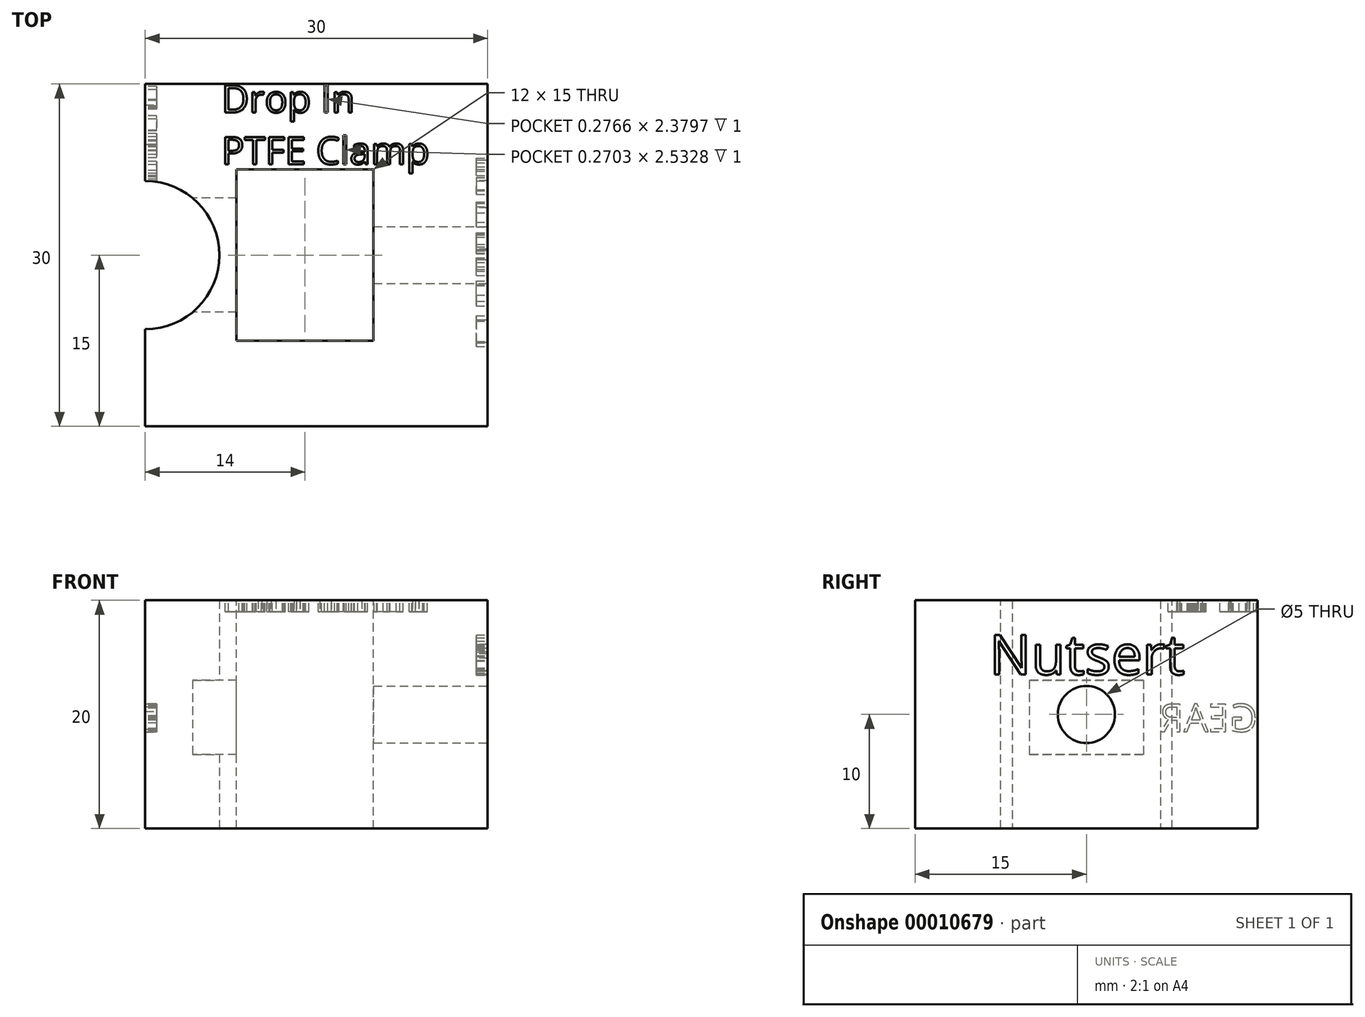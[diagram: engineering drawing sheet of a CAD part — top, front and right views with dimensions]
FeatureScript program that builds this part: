
annotation { "Feature Type Name" : "Feature", "Feature Type Description" : "" }
export const myFeature = defineFeature(function(context is Context, id is Id, definition is map)
    precondition{}
    {
        {
            var Q0;
            Q0=qCreatedBy(makeId("Top.planeOp"),FACE);
            var sketch = newSketch(context, id + "F0", { "sketchPlane" : qUnion([Q0])});
            skLineSegment(sketch, "E0.bottom", {"start": v(-15, 15) * mm, "end": v(15, 15) * mm});
            skLineSegment(sketch, "E0.top", {"start": v(-15, -15) * mm, "end": v(15, -15) * mm});
            skLineSegment(sketch, "E0.right", {"start": v(15, 15) * mm, "end": v(15, -15) * mm});
            skArc(sketch, "E1", {"start": v(-8.5, 0) * mm, "mid": v(-10.4, 4.6) * mm, "end": v(-15, 6.5) * mm});
            skArc(sketch, "E2", {"start": v(-15, -6.5) * mm, "mid": v(-10.4, -4.6) * mm, "end": v(-8.5, 0) * mm});
            skLineSegment(sketch, "E3", {"start": v(-15, 15) * mm, "end": v(-15, 6.5) * mm});
            skLineSegment(sketch, "E4", {"start": v(-15, -15) * mm, "end": v(-15, -6.5) * mm});
            skSolve(sketch);
        }
        {
            var Q0;
            Q0 = qSketchRegion(id + "F0", true);
            extrude(context, id + "F1", {"entities" : qUnion([Q0]), "depth" : 20 * mm});
        }
        {
            var Q0;
            Q0=makeQuery(id+"F1.opExtrude","CAP_FACE",FACE,{"disambiguationData":[OSD([sQuery(id+"F0.wireOp",EDGE,"E0.bottom"),sQuery(id+"F0.wireOp",EDGE,"E0.top"),sQuery(id+"F0.wireOp",EDGE,"E0.right"),sQuery(id+"F0.wireOp",EDGE,"E1"),sQuery(id+"F0.wireOp",EDGE,"E2"),sQuery(id+"F0.wireOp",EDGE,"E3"),sQuery(id+"F0.wireOp",EDGE,"E4")])],"isStart":false});
            var sketch = newSketch(context, id + "F2", { "sketchPlane" : qUnion([Q0])});
            skLineSegment(sketch, "E5.bottom", {"start": v(-7, 7.5) * mm, "end": v(5, 7.5) * mm});
            skLineSegment(sketch, "E5.top", {"start": v(-7, -7.5) * mm, "end": v(5, -7.5) * mm});
            skLineSegment(sketch, "E5.left", {"start": v(-7, 7.5) * mm, "end": v(-7, -7.5) * mm});
            skLineSegment(sketch, "E5.right", {"start": v(5, 7.5) * mm, "end": v(5, -7.5) * mm});
            skSolve(sketch);
        }
        {
            var Q0;
            Q0 = qSketchRegion(id + "F2", true);
            extrude(context, id + "F3", {"entities" : qUnion([Q0]), "operationType" : NewBodyOperationType.REMOVE, "endBound" : BoundingType.THROUGH_ALL, "oppositeDirection" : true, "depth" : 25 * mm});
        }
        {
            var Q0;
            Q0=makeQuery(id+"F1.opExtrude","SWEPT_FACE",FACE,{"disambiguationData":[OSD([sQuery(id+"F0.wireOp",EDGE,"E0.right")])]});
            var sketch = newSketch(context, id + "F4", { "sketchPlane" : qUnion([Q0])});
            skCircle(sketch, "E6", {"center": v(0, 10) * mm, "radius": 2.5 * mm});
            skSolve(sketch);
        }
        {
            var Q0;
            Q0 = qSketchRegion(id + "F4", true);
            var Q1;
            Q1=makeQuery(id+"F3.boolean.opBoolean","COPY",FACE,{"derivedFrom":makeQuery(id+"F3.opExtrude","SWEPT_FACE",FACE,{"disambiguationData":[OSD([sQuery(id+"F2.wireOp",EDGE,"E5.right")])]})});
            extrude(context, id + "F5", {"entities" : qUnion([Q0]), "operationType" : NewBodyOperationType.REMOVE, "endBound" : BoundingType.UP_TO_SURFACE, "oppositeDirection" : true, "endBoundEntityFace" : qUnion([Q1]), "depth" : 25 * mm});
        }
        {
            var Q0;
            Q0=makeQuery(id+"F1.opExtrude","SWEPT_FACE",FACE,{"disambiguationData":[OSD([sQuery(id+"F0.wireOp",EDGE,"E3")])]});
            var sketch = newSketch(context, id + "F6", { "sketchPlane" : qUnion([Q0])});
            skLineSegment(sketch, "E7.bottom", {"start": v(-5, 13) * mm, "end": v(5, 13) * mm});
            skLineSegment(sketch, "E7.top", {"start": v(-5, 6.5) * mm, "end": v(5, 6.5) * mm});
            skLineSegment(sketch, "E7.left", {"start": v(-5, 13) * mm, "end": v(-5, 6.5) * mm});
            skLineSegment(sketch, "E7.right", {"start": v(5, 13) * mm, "end": v(5, 6.5) * mm});
            skSolve(sketch);
        }
        {
            var Q0;
            Q0 = qSketchRegion(id + "F6", true);
            var Q1;
            Q1=makeQuery(id+"F3.boolean.opBoolean","COPY",FACE,{"derivedFrom":makeQuery(id+"F3.opExtrude","SWEPT_FACE",FACE,{"disambiguationData":[OSD([sQuery(id+"F2.wireOp",EDGE,"E5.left")])]})});
            extrude(context, id + "F7", {"entities" : qUnion([Q0]), "operationType" : NewBodyOperationType.REMOVE, "endBound" : BoundingType.UP_TO_SURFACE, "oppositeDirection" : true, "endBoundEntityFace" : qUnion([Q1]), "depth" : 25 * mm});
        }
        {
            var Q0;
            Q0=makeQuery(id+"F1.opExtrude","SWEPT_FACE",FACE,{"disambiguationData":[OSD([sQuery(id+"F0.wireOp",EDGE,"E0.right")])]});
            var sketch = newSketch(context, id + "F8", { "sketchPlane" : qUnion([Q0])});
            skText(sketch, "E8", { "text": "Nutsert\n", "fontName": "OpenSans-Regular.ttf"});
            const initialGuessF8  = {"E8": [-0.0085, 0.0135, 1, 0, 0.0035]};
            skSetInitialGuess(sketch, initialGuessF8);
            skSolve(sketch);
        }
        {
            var Q0;
            Q0 = qSketchRegion(id + "F8", true);
            extrude(context, id + "F9", {"entities" : qUnion([Q0]), "operationType" : NewBodyOperationType.REMOVE, "oppositeDirection" : true, "depth" : 1 * mm});
        }
        {
            var Q0;
            Q0=makeQuery(id+"F1.opExtrude","SWEPT_FACE",FACE,{"disambiguationData":[OSD([sQuery(id+"F0.wireOp",EDGE,"E3")])]});
            var sketch = newSketch(context, id + "F10", { "sketchPlane" : qUnion([Q0])});
            skText(sketch, "E9", { "text": "GEAR", "fontName": "OpenSans-Regular.ttf"});
            const initialGuessF10  = {"E9": [-0.015, 0.0085, 1, 0, 0.00243]};
            skSetInitialGuess(sketch, initialGuessF10);
            skSolve(sketch);
        }
        {
            var Q0;
            Q0 = qSketchRegion(id + "F10", true);
            extrude(context, id + "F11", {"entities" : qUnion([Q0]), "operationType" : NewBodyOperationType.REMOVE, "oppositeDirection" : true, "depth" : 1 * mm});
        }
        {
            var Q0;
            Q0=makeQuery(id+"F1.opExtrude","CAP_FACE",FACE,{"disambiguationData":[OSD([sQuery(id+"F0.wireOp",EDGE,"E0.bottom"),sQuery(id+"F0.wireOp",EDGE,"E0.top"),sQuery(id+"F0.wireOp",EDGE,"E0.right"),sQuery(id+"F0.wireOp",EDGE,"E1"),sQuery(id+"F0.wireOp",EDGE,"E2"),sQuery(id+"F0.wireOp",EDGE,"E3"),sQuery(id+"F0.wireOp",EDGE,"E4")])],"isStart":false});
            var sketch = newSketch(context, id + "F12", { "sketchPlane" : qUnion([Q0])});
            skText(sketch, "E10", { "text": "Drop In \nPTFE Clamp", "fontName": "OpenSans-Regular.ttf"});
            const initialGuessF12  = {"E10": [-0.00833, 0.0125, 1, 0, 0.0024]};
            skSetInitialGuess(sketch, initialGuessF12);
            skSolve(sketch);
        }
        {
            var Q0;
            Q0 = qSketchRegion(id + "F12", true);
            extrude(context, id + "F13", {"entities" : qUnion([Q0]), "operationType" : NewBodyOperationType.REMOVE, "oppositeDirection" : true, "depth" : 1 * mm});
        }
    });
